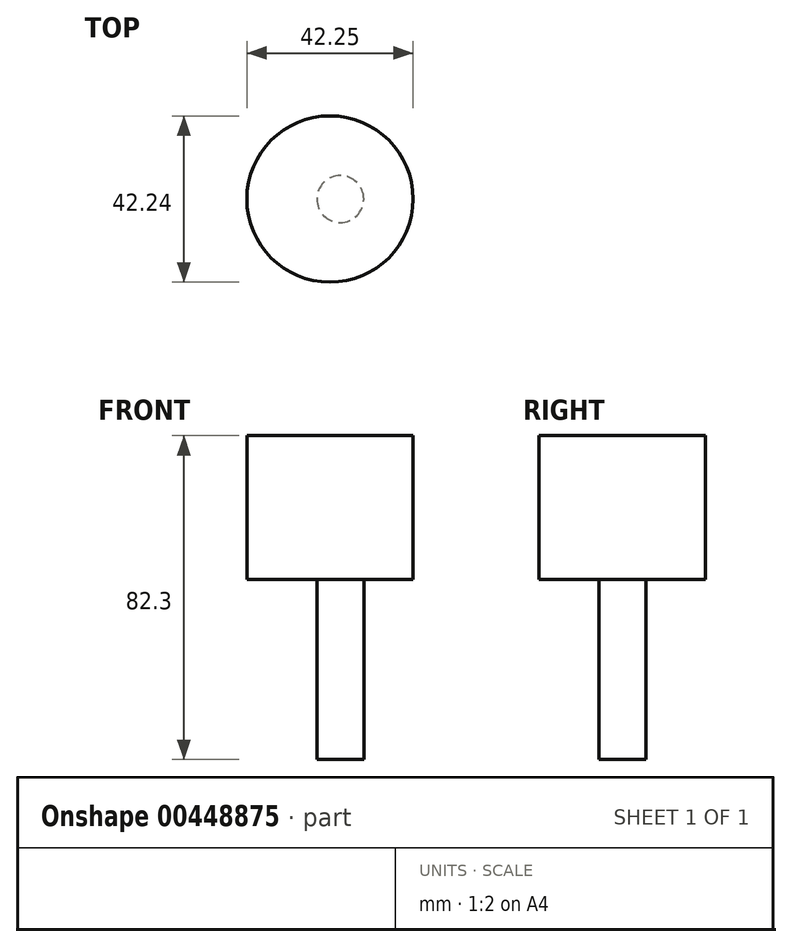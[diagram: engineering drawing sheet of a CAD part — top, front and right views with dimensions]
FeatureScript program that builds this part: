
annotation { "Feature Type Name" : "Feature", "Feature Type Description" : "" }
export const myFeature = defineFeature(function(context is Context, id is Id, definition is map)
    precondition{}
    {
        {
            var Q0;
            Q0=qCreatedBy(makeId("Top.planeOp"),FACE);
            var sketch = newSketch(context, id + "F0", { "sketchPlane" : qUnion([Q0])});
            skCircle(sketch, "E0", {"center": v(7.38, 0) * mm, "radius": 21.12 * mm});
            skSolve(sketch);
        }
        {
            var Q0;
            Q0=makeQuery(id+"F0.imprint","IMPRINT",FACE,{"disambiguationData":[TD([[makeQuery(id+"F0.imprint","IMPRINT",EDGE,{"derivedFrom":sQuery(id+"F0.wireOp",EDGE,"E0")}),1.0]])]});
            extrude(context, id + "F1", {"entities" : qUnion([Q0]), "depth" : 36.58 * mm});
        }
        {
            var Q0;
            Q0=makeQuery(id+"F1.opExtrude","CAP_FACE",FACE,{"disambiguationData":[OSD([sQuery(id+"F0.wireOp",EDGE,"E0")])],"isStart":false});
            var sketch = newSketch(context, id + "F2", { "sketchPlane" : qUnion([Q0])});
            skCircle(sketch, "E1", {"center": v(10, 0) * mm, "radius": 5.97 * mm});
            skSolve(sketch);
        }
        {
            var Q0;
            Q0=makeQuery(id+"F2.imprint","IMPRINT",FACE,{"disambiguationData":[TD([[makeQuery(id+"F2.imprint","IMPRINT",EDGE,{"derivedFrom":sQuery(id+"F2.wireOp",EDGE,"E1")}),1.0]])]});
            extrude(context, id + "F3", {"entities" : qUnion([Q0]), "operationType" : NewBodyOperationType.ADD, "oppositeDirection" : true, "depth" : 82.3 * mm});
        }
    });
